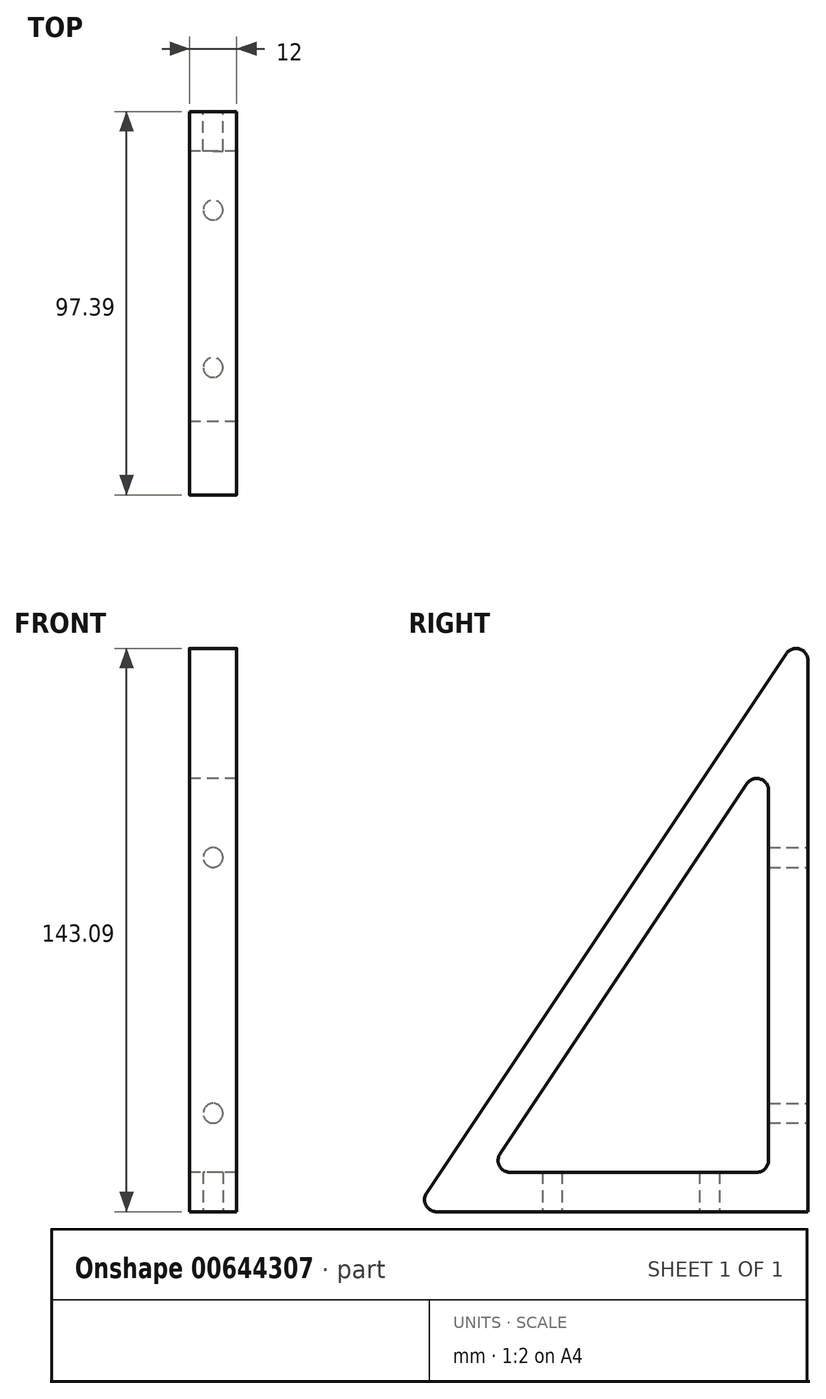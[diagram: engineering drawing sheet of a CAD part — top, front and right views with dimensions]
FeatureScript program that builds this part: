
annotation { "Feature Type Name" : "Feature", "Feature Type Description" : "" }
export const myFeature = defineFeature(function(context is Context, id is Id, definition is map)
    precondition{}
    {
        {
            var Q0;
            Q0=qCreatedBy(makeId("Right.planeOp"),FACE);
            var sketch = newSketch(context, id + "F0", { "sketchPlane" : qUnion([Q0])});
            skLineSegment(sketch, "E0", {"start": v(-100, 0) * mm, "end": v(0, 0) * mm});
            skLineSegment(sketch, "E1", {"start": v(0, 0) * mm, "end": v(0, 150) * mm});
            skLineSegment(sketch, "E2", {"start": v(-100, 0) * mm, "end": v(0, 150) * mm});
            skLineSegment(sketch, "E3.0", {"start": v(-81.31, 10) * mm, "end": v(-10, 116.97) * mm});
            skLineSegment(sketch, "E3.1", {"start": v(-81.31, 10) * mm, "end": v(-10, 10) * mm});
            skLineSegment(sketch, "E3.2", {"start": v(-10, 10) * mm, "end": v(-10, 116.97) * mm});
            skSolve(sketch);
        }
        {
            var Q0;
            Q0 = qSketchRegion(id + "F0", true);
            extrude(context, id + "F1", {"entities" : qUnion([Q0]), "endBound" : BoundingType.SYMMETRIC, "depth" : 12 * mm, "offsetDistance" : 25 * mm});
        }
        {
            var Q0;
            Q0=makeQuery(id+"F1.opExtrude","SWEPT_EDGE",EDGE,{"disambiguationData":[OSD([sQuery(id+"F0.wireOp",EDGE,"E0"),sQuery(id+"F0.wireOp",EDGE,"E2")])]});
            var Q1;
            Q1=makeQuery(id+"F1.opExtrude","SWEPT_EDGE",EDGE,{"disambiguationData":[OSD([sQuery(id+"F0.wireOp",EDGE,"E1"),sQuery(id+"F0.wireOp",EDGE,"E2")])]});
            var Q2;
            Q2=makeQuery(id+"F1.opExtrude","SWEPT_EDGE",EDGE,{"disambiguationData":[OSD([sQuery(id+"F0.wireOp",EDGE,"E3.0"),sQuery(id+"F0.wireOp",EDGE,"E3.2")])]});
            var Q3;
            Q3=makeQuery(id+"F1.opExtrude","SWEPT_EDGE",EDGE,{"disambiguationData":[OSD([sQuery(id+"F0.wireOp",EDGE,"E3.1"),sQuery(id+"F0.wireOp",EDGE,"E3.2")])]});
            var Q4;
            Q4=makeQuery(id+"F1.opExtrude","SWEPT_EDGE",EDGE,{"disambiguationData":[OSD([sQuery(id+"F0.wireOp",EDGE,"E3.0"),sQuery(id+"F0.wireOp",EDGE,"E3.1")])]});
            fillet(context, id + "F2", {"entities" : qUnion([Q0, Q1, Q2, Q3, Q4]), "radius" : 3 * mm, "tangentPropagation" : true, "allowEdgeOverflow" : false});
        }
        {
            var Q0;
            Q0=makeQuery(id+"F1.opExtrude","SWEPT_FACE",FACE,{"disambiguationData":[OSD([sQuery(id+"F0.wireOp",EDGE,"E1")])]});
            var sketch = newSketch(context, id + "F3", { "sketchPlane" : qUnion([Q0])});
            skLineSegment(sketch, "E4", {"start": v(0, 97.89) * mm, "end": v(0, -7.2) * mm, "construction": true});
            skCircle(sketch, "E5", {"center": v(0, 90) * mm, "radius": 2.5 * mm});
            skCircle(sketch, "E6", {"center": v(0, 25) * mm, "radius": 2.5 * mm});
            skSolve(sketch);
        }
        {
            var Q0;
            Q0 = qSketchRegion(id + "F3", true);
            extrude(context, id + "F4", {"entities" : qUnion([Q0]), "operationType" : NewBodyOperationType.REMOVE, "endBound" : BoundingType.UP_TO_NEXT, "oppositeDirection" : true, "depth" : 25 * mm, "offsetDistance" : 25 * mm});
        }
        {
            var Q0;
            Q0=makeQuery(id+"F1.opExtrude","SWEPT_FACE",FACE,{"disambiguationData":[OSD([sQuery(id+"F0.wireOp",EDGE,"E0")])]});
            var sketch = newSketch(context, id + "F5", { "sketchPlane" : qUnion([Q0])});
            skLineSegment(sketch, "E7", {"start": v(0, 12.28) * mm, "end": v(0, 86.4) * mm, "construction": true});
            skCircle(sketch, "E8", {"center": v(0, 25) * mm, "radius": 2.5 * mm});
            skCircle(sketch, "E9", {"center": v(0, 65) * mm, "radius": 2.5 * mm});
            skSolve(sketch);
        }
        {
            var Q0;
            Q0 = qSketchRegion(id + "F5", true);
            extrude(context, id + "F6", {"entities" : qUnion([Q0]), "operationType" : NewBodyOperationType.REMOVE, "endBound" : BoundingType.UP_TO_NEXT, "oppositeDirection" : true, "depth" : 25 * mm, "offsetDistance" : 25 * mm});
        }
    });
